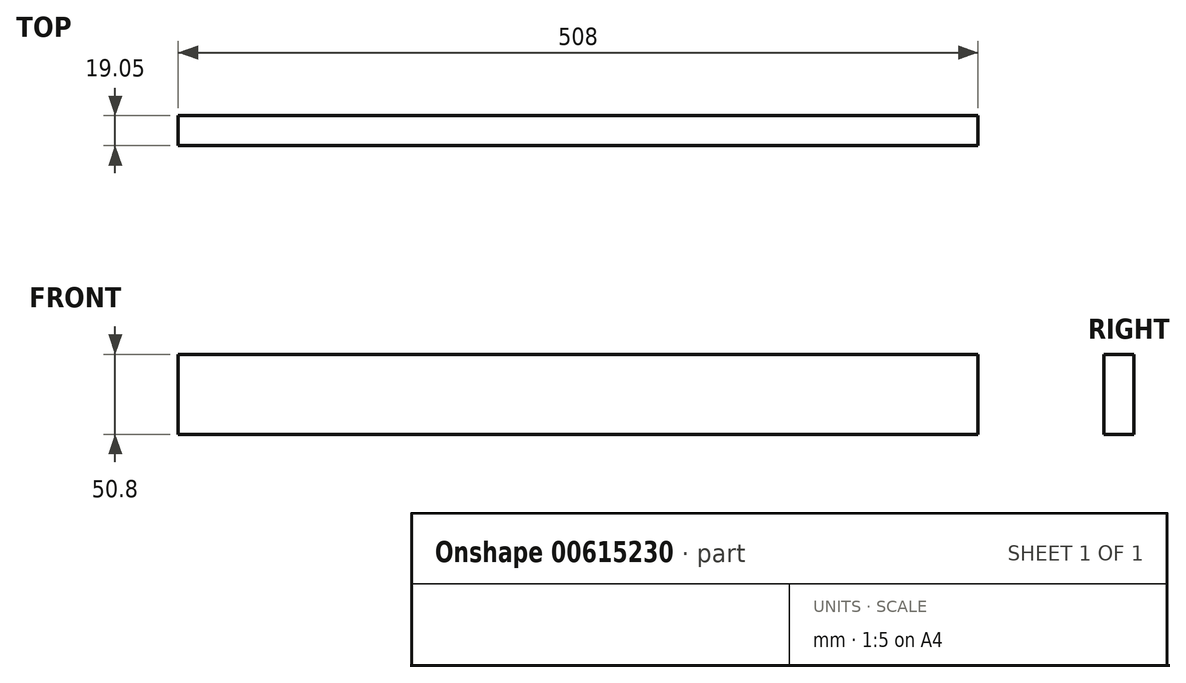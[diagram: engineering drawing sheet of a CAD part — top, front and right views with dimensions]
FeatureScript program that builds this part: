
annotation { "Feature Type Name" : "Feature", "Feature Type Description" : "" }
export const myFeature = defineFeature(function(context is Context, id is Id, definition is map)
    precondition{}
    {
        {
            var Q0;
            Q0=qCreatedBy(makeId("Front.planeOp"),FACE);
            var sketch = newSketch(context, id + "F0", { "sketchPlane" : qUnion([Q0])});
            skLineSegment(sketch, "E0.bottom", {"start": v(508, 50.8) * mm, "end": v(0, 50.8) * mm});
            skLineSegment(sketch, "E0.top", {"start": v(508, 0) * mm, "end": v(0, 0) * mm});
            skLineSegment(sketch, "E0.left", {"start": v(508, 50.8) * mm, "end": v(508, 0) * mm});
            skLineSegment(sketch, "E0.right", {"start": v(0, 50.8) * mm, "end": v(0, 0) * mm});
            skSolve(sketch);
        }
        {
            var Q0;
            Q0=makeQuery(id+"F0.imprint","IMPRINT",FACE,{"disambiguationData":[TD([[makeQuery(id+"F0.imprint","IMPRINT",EDGE,{"derivedFrom":sQuery(id+"F0.wireOp",EDGE,"E0.bottom")}),1.0]])]});
            extrude(context, id + "F1", {"entities" : qUnion([Q0]), "depth" : 19.05 * mm, "offsetDistance" : 25.4 * mm});
        }
    });
